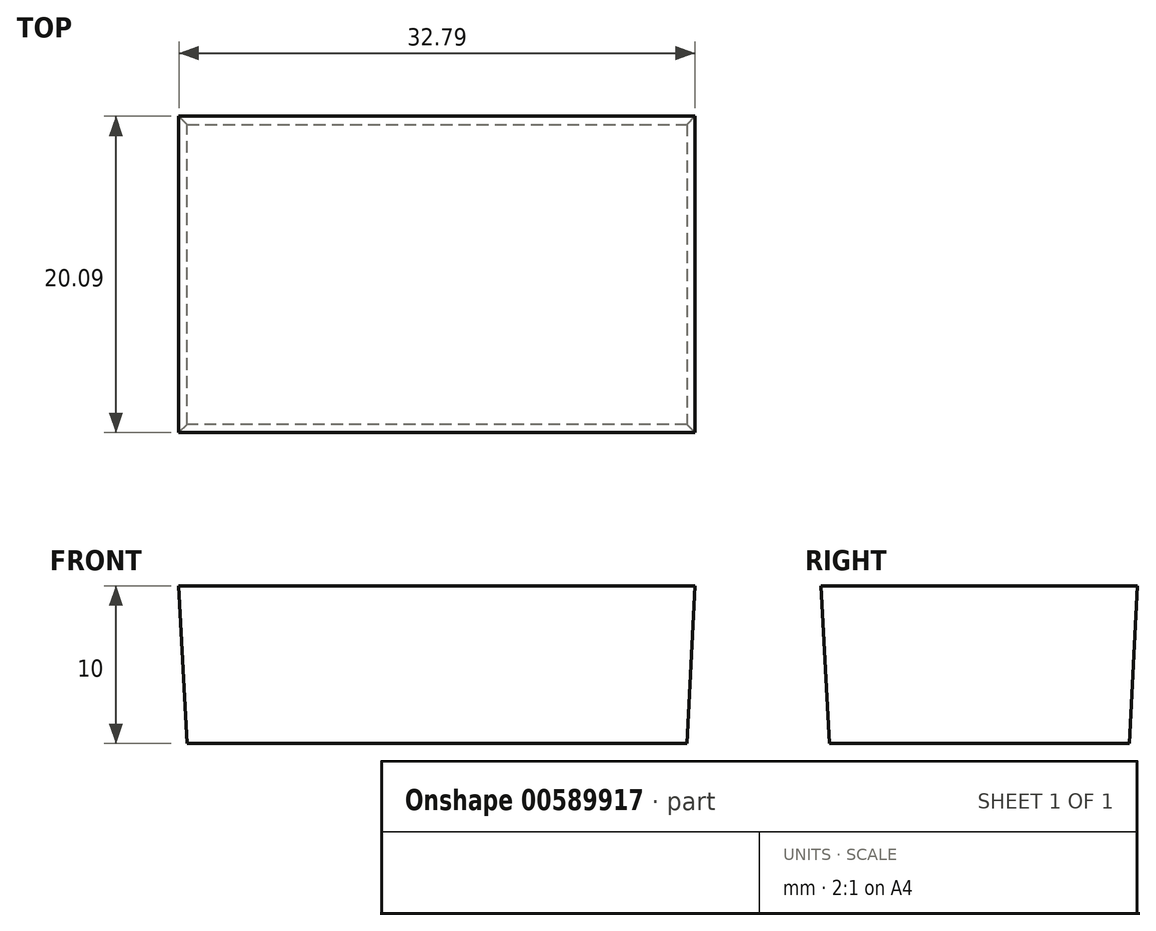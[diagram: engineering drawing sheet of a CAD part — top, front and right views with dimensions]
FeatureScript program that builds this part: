
annotation { "Feature Type Name" : "Feature", "Feature Type Description" : "" }
export const myFeature = defineFeature(function(context is Context, id is Id, definition is map)
    precondition{}
    {
        {
            assignVariable(context, id + "F0", {"name" : "t", "anyValue" : 10 * mm});
        }
        {
            var Q0;
            Q0=qCreatedBy(makeId("Top.planeOp"),FACE);
            var sketch = newSketch(context, id + "F1", { "sketchPlane" : qUnion([Q0])});
            skLineSegment(sketch, "E0.bottom", {"start": v(-31.75, 19.05) * mm, "end": v(0, 19.05) * mm});
            skLineSegment(sketch, "E0.top", {"start": v(-31.75, 0) * mm, "end": v(0, 0) * mm});
            skLineSegment(sketch, "E0.left", {"start": v(-31.75, 19.05) * mm, "end": v(-31.75, 0) * mm});
            skLineSegment(sketch, "E0.right", {"start": v(0, 19.05) * mm, "end": v(0, 0) * mm});
            skSolve(sketch);
        }
        {
            var Q0;
            Q0 = qSketchRegion(id + "F1", true);
            extrude(context, id + "F2", {"entities" : qUnion([Q0]), "depth" : getVariable(context, 't'), "offsetDistance" : 25.4 * mm, "hasDraft" : true, "draftAngle" : 3 * degree});
        }
    });
